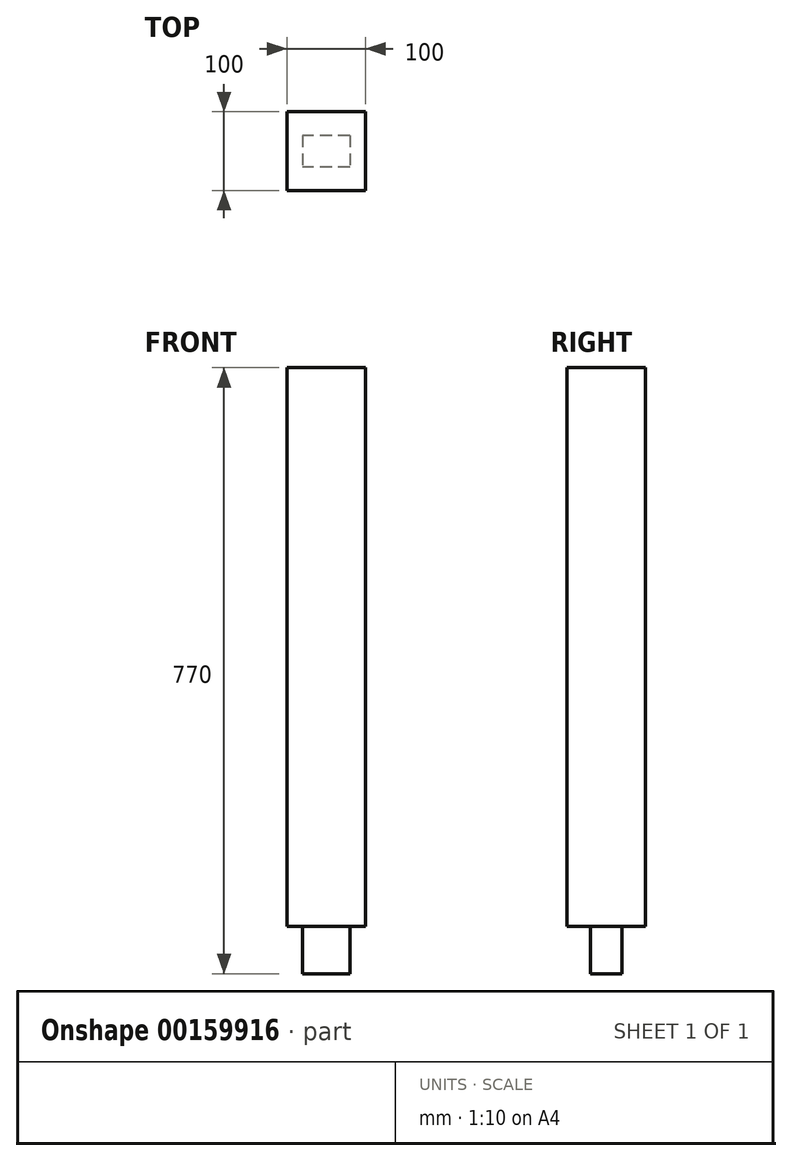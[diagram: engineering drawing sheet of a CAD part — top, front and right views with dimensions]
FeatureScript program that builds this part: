
annotation { "Feature Type Name" : "Feature", "Feature Type Description" : "" }
export const myFeature = defineFeature(function(context is Context, id is Id, definition is map)
    precondition{}
    {
        {
            assignVariable(context, id + "F0", {"name" : "L", "anyValue" : 750 * mm + 20 * mm});
        }
        {
            assignVariable(context, id + "F1", {"name" : "Feder", "anyValue" : 60 * mm});
        }
        {
            var Q0;
            Q0=qCreatedBy(makeId("Top.planeOp"),FACE);
            var sketch = newSketch(context, id + "F2", { "sketchPlane" : qUnion([Q0])});
            skLineSegment(sketch, "E0.bottom", {"start": v(50, -50) * mm, "end": v(-50, -50) * mm});
            skLineSegment(sketch, "E0.top", {"start": v(50, 50) * mm, "end": v(-50, 50) * mm});
            skLineSegment(sketch, "E0.left", {"start": v(50, -50) * mm, "end": v(50, 50) * mm});
            skLineSegment(sketch, "E0.right", {"start": v(-50, -50) * mm, "end": v(-50, 50) * mm});
            skPoint(sketch, "E0.middle", {"position": v(0, 0) * mm});
            skSolve(sketch);
        }
        {
            var Q0;
            Q0 = qSketchRegion(id + "F2", true);
            extrude(context, id + "F3", {"entities" : qUnion([Q0]), "depth" : getVariable(context, 'L') - getVariable(context, 'Feder')});
        }
        {
            var Q0;
            Q0=qCreatedBy(makeId("Top.planeOp"),FACE);
            var sketch = newSketch(context, id + "F4", { "sketchPlane" : qUnion([Q0])});
            skLineSegment(sketch, "E1.bottom", {"start": v(30, 20) * mm, "end": v(-30, 20) * mm});
            skLineSegment(sketch, "E1.top", {"start": v(30, -20) * mm, "end": v(-30, -20) * mm});
            skLineSegment(sketch, "E1.left", {"start": v(30, 20) * mm, "end": v(30, -20) * mm});
            skLineSegment(sketch, "E1.right", {"start": v(-30, 20) * mm, "end": v(-30, -20) * mm});
            skPoint(sketch, "E1.middle", {"position": v(0, 0) * mm});
            skSolve(sketch);
        }
        {
            var Q0;
            Q0 = qSketchRegion(id + "F4", true);
            extrude(context, id + "F5", {"entities" : qUnion([Q0]), "operationType" : NewBodyOperationType.ADD, "oppositeDirection" : true, "depth" : getVariable(context, 'Feder')});
        }
    });
